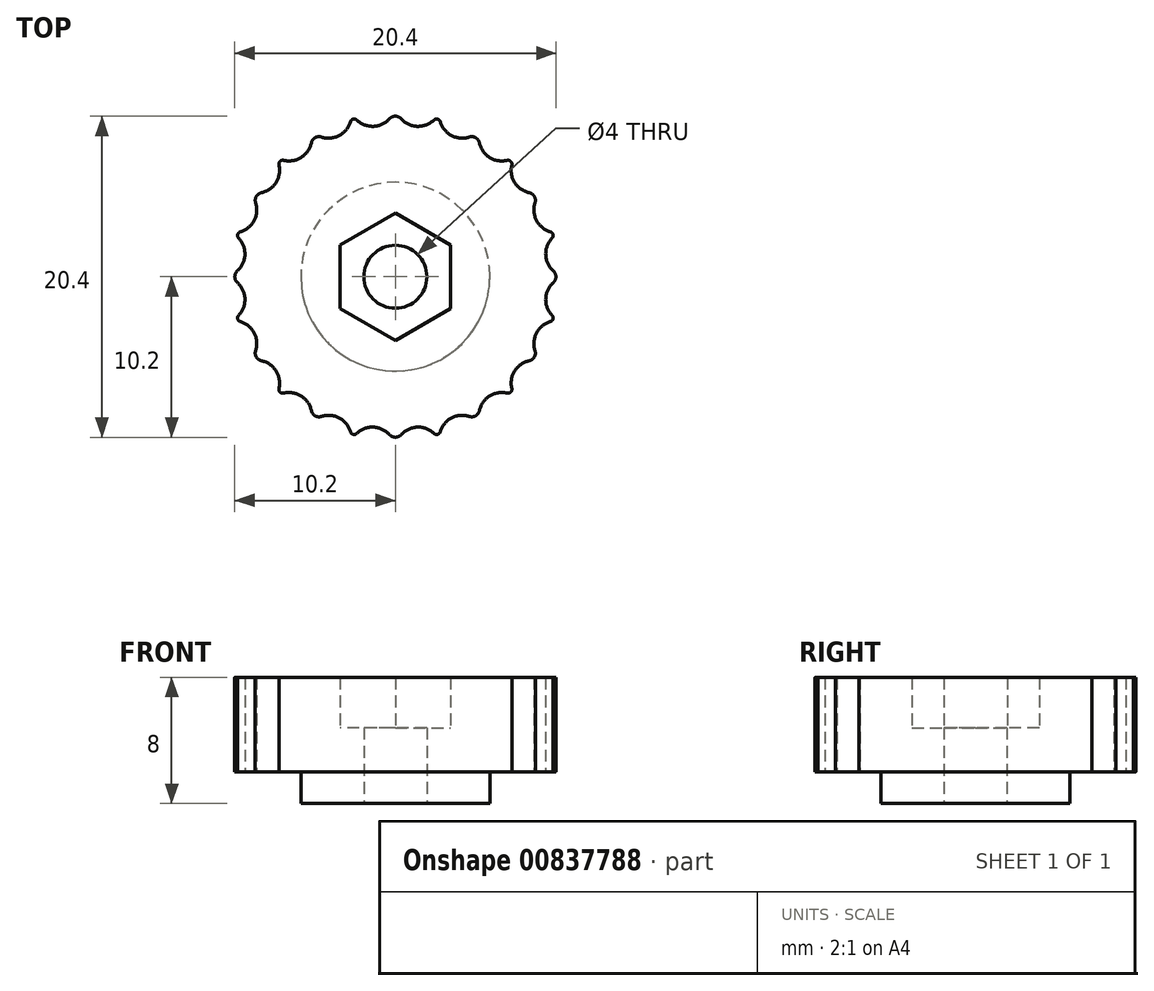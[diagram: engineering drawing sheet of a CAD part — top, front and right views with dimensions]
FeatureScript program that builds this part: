
annotation { "Feature Type Name" : "Feature", "Feature Type Description" : "" }
export const myFeature = defineFeature(function(context is Context, id is Id, definition is map)
    precondition{}
    {
        {
            var Q0;
            Q0=qCreatedBy(makeId("Top.planeOp"),FACE);
            var sketch = newSketch(context, id + "F0", { "sketchPlane" : qUnion([Q0])});
            skLineSegment(sketch, "E0", {"start": v(0, 0) * mm, "end": v(-11, 0) * mm});
            skLineSegment(sketch, "E1", {"start": v(0, 0) * mm, "end": v(0, 11) * mm});
            skLineSegment(sketch, "E2", {"start": v(0, 0) * mm, "end": v(-10.63, 2.85) * mm, "construction": true});
            skLineSegment(sketch, "E3", {"start": v(0, 0) * mm, "end": v(-9.53, 5.5) * mm, "construction": true});
            skLineSegment(sketch, "E4", {"start": v(0, 0) * mm, "end": v(-7.78, 7.78) * mm, "construction": true});
            skLineSegment(sketch, "E5", {"start": v(0, 0) * mm, "end": v(-2.85, 10.63) * mm, "construction": true});
            skLineSegment(sketch, "E6", {"start": v(0, 0) * mm, "end": v(-5.5, 9.53) * mm, "construction": true});
            skArc(sketch, "E7", {"start": v(-11, 0) * mm, "mid": v(-9.56, 1.26) * mm, "end": v(-10.63, 2.85) * mm});
            skArc(sketch, "E8", {"start": v(-7.78, 7.78) * mm, "mid": v(-5.87, 7.65) * mm, "end": v(-5.5, 9.53) * mm});
            skArc(sketch, "E9", {"start": v(-5.5, 9.53) * mm, "mid": v(-3.7, 8.91) * mm, "end": v(-2.85, 10.63) * mm});
            skArc(sketch, "E10", {"start": v(-2.85, 10.63) * mm, "mid": v(-1.26, 9.56) * mm, "end": v(0, 11) * mm});
            skArc(sketch, "E11", {"start": v(-10.63, 2.85) * mm, "mid": v(-8.91, 3.7) * mm, "end": v(-9.53, 5.5) * mm});
            skArc(sketch, "E12", {"start": v(-9.53, 5.5) * mm, "mid": v(-7.65, 5.87) * mm, "end": v(-7.78, 7.78) * mm});
            skLineSegment(sketch, "E13", {"start": v(0, 0) * mm, "end": v(-3.5, 0) * mm, "construction": true});
            skLineSegment(sketch, "E14", {"start": v(0, 0) * mm, "end": v(0, 4.04) * mm, "construction": true});
            skArc(sketch, "E15", {"start": v(0, 4.04) * mm, "mid": v(-2.86, 2.86) * mm, "end": v(-4.04, 0) * mm, "construction": true});
            skPoint(sketch, "E16", {"position": v(-3.5, 2.02) * mm});
            skLineSegment(sketch, "E17", {"start": v(0, 4.04) * mm, "end": v(-3.5, 2.02) * mm});
            skLineSegment(sketch, "E18", {"start": v(-3.5, 0) * mm, "end": v(-3.5, 2.02) * mm});
            skArc(sketch, "E19", {"start": v(0, 2) * mm, "mid": v(-1.41, 1.41) * mm, "end": v(-2, 0) * mm});
            skSolve(sketch);
        }
        {
            var Q0;
            {var subQ0=sQuery(id+"F0.wireOp",EDGE,"E7");Q0=makeQuery(id+"F0.imprint","IMPRINT",FACE,{"disambiguationData":[TD([[makeQuery(id+"F0.imprint","IMPRINT",EDGE,{"derivedFrom":subQ0}),-1.0]])]});}
            extrude(context, id + "F1", {"entities" : qUnion([Q0]), "depth" : 6 * mm, "offsetDistance" : 25 * mm});
        }
        {
            var Q0;
            {var subQ1=sQuery(id+"F0.wireOp",EDGE,"E17");Q0=makeQuery(id+"F0.imprint","IMPRINT",FACE,{"disambiguationData":[TD([[makeQuery(id+"F0.imprint","IMPRINT",EDGE,{"derivedFrom":subQ1}),1.0]])]});}
            extrude(context, id + "F2", {"entities" : qUnion([Q0]), "operationType" : NewBodyOperationType.ADD, "depth" : 2.8 * mm, "offsetDistance" : 25 * mm});
        }
        {
            var Q0;
            Q0=makeQuery(id+"F1.opExtrude","SWEPT_EDGE",EDGE,{"disambiguationData":[OSD([sQuery(id+"F0.wireOp",EDGE,"E9"),sQuery(id+"F0.wireOp",EDGE,"E10")])]});
            var Q1;
            Q1=makeQuery(id+"F1.opExtrude","SWEPT_EDGE",EDGE,{"disambiguationData":[OSD([sQuery(id+"F0.wireOp",EDGE,"E8"),sQuery(id+"F0.wireOp",EDGE,"E12")])]});
            var Q2;
            Q2=makeQuery(id+"F1.opExtrude","SWEPT_EDGE",EDGE,{"disambiguationData":[OSD([sQuery(id+"F0.wireOp",EDGE,"E7"),sQuery(id+"F0.wireOp",EDGE,"E11")])]});
            fillet(context, id + "F3", {"entities" : qUnion([Q0, Q1, Q2]), "radius" : .25 * mm, "tangentPropagation" : true, "allowEdgeOverflow" : false});
        }
        {
            var Q0;
            Q0=makeQuery(id+"F1.opExtrude","SWEPT_EDGE",EDGE,{"disambiguationData":[OSD([sQuery(id+"F0.wireOp",EDGE,"E8"),sQuery(id+"F0.wireOp",EDGE,"E9")])]});
            var Q1;
            Q1=makeQuery(id+"F1.opExtrude","SWEPT_EDGE",EDGE,{"disambiguationData":[OSD([sQuery(id+"F0.wireOp",EDGE,"E11"),sQuery(id+"F0.wireOp",EDGE,"E12")])]});
            fillet(context, id + "F4", {"entities" : qUnion([Q0, Q1]), "radius" : .5 * mm, "tangentPropagation" : true, "allowEdgeOverflow" : false});
        }
        {
            var Q0;
            Q0=makeQuery(id+"F1.opExtrude","SWEPT_BODY",BODY,{"disambiguationData":[OSD([sQuery(id+"F0.wireOp",EDGE,"E0"),sQuery(id+"F0.wireOp",EDGE,"E1"),sQuery(id+"F0.wireOp",EDGE,"E7"),sQuery(id+"F0.wireOp",EDGE,"E8"),sQuery(id+"F0.wireOp",EDGE,"E9"),sQuery(id+"F0.wireOp",EDGE,"E10"),sQuery(id+"F0.wireOp",EDGE,"E11"),sQuery(id+"F0.wireOp",EDGE,"E12"),sQuery(id+"F0.wireOp",EDGE,"E17"),sQuery(id+"F0.wireOp",EDGE,"E18")])]});
            var Q1;
            {var subQ0=sQuery(id+"F0.wireOp",EDGE,"E0");Q1=makeQuery(id+"F2.boolean.opBoolean","MERGE",FACE,{"derivedFrom":[makeQuery(id+"F1.opExtrude","SWEPT_FACE",FACE,{"disambiguationData":[OSD([subQ0])]}),makeQuery(id+"F2.opExtrude","SWEPT_FACE",FACE,{"disambiguationData":[OSD([subQ0])]})]});}
            mirror(context, id + "F5", {"operationType" : NewBodyOperationType.ADD, "entities" : qUnion([Q0]), "mirrorPlane" : qUnion([Q1])});
        }
        {
            var Q0;
            Q0=makeQuery(id+"F1.opExtrude","SWEPT_BODY",BODY,{"disambiguationData":[OSD([sQuery(id+"F0.wireOp",EDGE,"E0"),sQuery(id+"F0.wireOp",EDGE,"E1"),sQuery(id+"F0.wireOp",EDGE,"E7"),sQuery(id+"F0.wireOp",EDGE,"E8"),sQuery(id+"F0.wireOp",EDGE,"E9"),sQuery(id+"F0.wireOp",EDGE,"E10"),sQuery(id+"F0.wireOp",EDGE,"E11"),sQuery(id+"F0.wireOp",EDGE,"E12"),sQuery(id+"F0.wireOp",EDGE,"E17"),sQuery(id+"F0.wireOp",EDGE,"E18")])]});
            var Q1;
            {var subQ0=sQuery(id+"F0.wireOp",EDGE,"E1");Q1=makeQuery(id+"F5.opPattern","COPY",FACE,{"derivedFrom":makeQuery(id+"F2.boolean.opBoolean","MERGE",FACE,{"derivedFrom":[makeQuery(id+"F1.opExtrude","SWEPT_FACE",FACE,{"disambiguationData":[OSD([subQ0])]}),makeQuery(id+"F2.opExtrude","SWEPT_FACE",FACE,{"disambiguationData":[OSD([subQ0])]})]}),"instanceName":"1"});}
            mirror(context, id + "F6", {"operationType" : NewBodyOperationType.ADD, "entities" : qUnion([Q0]), "mirrorPlane" : qUnion([Q1])});
        }
        {
            var Q0;
            {var subQ0=makeQuery(id+"F5.opPattern","COPY",EDGE,{"derivedFrom":makeQuery(id+"F1.opExtrude","SWEPT_EDGE",EDGE,{"disambiguationData":[OSD([sQuery(id+"F0.wireOp",EDGE,"E1"),sQuery(id+"F0.wireOp",EDGE,"E10")])]}),"instanceName":"1"});Q0=makeQuery(id+"F6.boolean.opBoolean","MERGE",EDGE,{"derivedFrom":[subQ0,makeQuery(id+"F6.opPattern","COPY",EDGE,{"derivedFrom":subQ0,"instanceName":"1"})]});}
            var Q1;
            {var subQ0=makeQuery(id+"F1.opExtrude","SWEPT_EDGE",EDGE,{"disambiguationData":[OSD([sQuery(id+"F0.wireOp",EDGE,"E0"),sQuery(id+"F0.wireOp",EDGE,"E7")])]});Q1=makeQuery(id+"F6.opPattern","COPY",EDGE,{"derivedFrom":makeQuery(id+"F5.boolean.opBoolean","MERGE",EDGE,{"derivedFrom":[subQ0,makeQuery(id+"F5.opPattern","COPY",EDGE,{"derivedFrom":subQ0,"instanceName":"1"})]}),"instanceName":"1"});}
            var Q2;
            {var subQ0=makeQuery(id+"F1.opExtrude","SWEPT_EDGE",EDGE,{"disambiguationData":[OSD([sQuery(id+"F0.wireOp",EDGE,"E1"),sQuery(id+"F0.wireOp",EDGE,"E10")])]});Q2=makeQuery(id+"F6.boolean.opBoolean","MERGE",EDGE,{"derivedFrom":[subQ0,makeQuery(id+"F6.opPattern","COPY",EDGE,{"derivedFrom":subQ0,"instanceName":"1"})]});}
            var Q3;
            {var subQ0=makeQuery(id+"F1.opExtrude","SWEPT_EDGE",EDGE,{"disambiguationData":[OSD([sQuery(id+"F0.wireOp",EDGE,"E0"),sQuery(id+"F0.wireOp",EDGE,"E7")])]});Q3=makeQuery(id+"F5.boolean.opBoolean","MERGE",EDGE,{"derivedFrom":[subQ0,makeQuery(id+"F5.opPattern","COPY",EDGE,{"derivedFrom":subQ0,"instanceName":"1"})]});}
            fillet(context, id + "F7", {"entities" : qUnion([Q0, Q1, Q2, Q3]), "radius" : .5 * mm, "tangentPropagation" : true, "allowEdgeOverflow" : false});
        }
        {
            var Q0;
            {var subQ0=sQuery(id+"F0.wireOp",EDGE,"E18");var subQ1=sQuery(id+"F0.wireOp",EDGE,"E17");var subQ2=sQuery(id+"F0.wireOp",EDGE,"E1");var subQ3=sQuery(id+"F0.wireOp",EDGE,"E0");var subQ4=makeQuery(id+"F2.boolean.opBoolean","MERGE",FACE,{"derivedFrom":[makeQuery(id+"F1.opExtrude","CAP_FACE",FACE,{"disambiguationData":[OSD([subQ3,subQ2,sQuery(id+"F0.wireOp",EDGE,"E7"),sQuery(id+"F0.wireOp",EDGE,"E8"),sQuery(id+"F0.wireOp",EDGE,"E9"),sQuery(id+"F0.wireOp",EDGE,"E10"),sQuery(id+"F0.wireOp",EDGE,"E11"),sQuery(id+"F0.wireOp",EDGE,"E12"),subQ1,subQ0])],"isStart":true}),makeQuery(id+"F2.opExtrude","CAP_FACE",FACE,{"disambiguationData":[OSD([subQ3,subQ2,subQ1,subQ0,sQuery(id+"F0.wireOp",EDGE,"E19")])],"isStart":true})]});var subQ5=makeQuery(id+"F5.boolean.opBoolean","MERGE",FACE,{"derivedFrom":[subQ4,makeQuery(id+"F5.opPattern","COPY",FACE,{"derivedFrom":subQ4,"instanceName":"1"})]});Q0=makeQuery(id+"F6.boolean.opBoolean","MERGE",FACE,{"derivedFrom":[subQ5,makeQuery(id+"F6.opPattern","COPY",FACE,{"derivedFrom":subQ5,"instanceName":"1"})]});}
            var sketch = newSketch(context, id + "F8", { "sketchPlane" : qUnion([Q0])});
            skCircle(sketch, "E20", {"center": v(0, 0) * mm, "radius": 6 * mm});
            skSolve(sketch);
        }
        {
            var Q0;
            Q0=makeQuery(id+"F8.imprint","IMPRINT",FACE,{"disambiguationData":[TD([[makeQuery(id+"F8.imprint","IMPRINT",EDGE,{"derivedFrom":sQuery(id+"F8.wireOp",EDGE,"E20")}),1.0]])]});
            extrude(context, id + "F9", {"entities" : qUnion([Q0]), "operationType" : NewBodyOperationType.ADD, "depth" : 2 * mm, "offsetDistance" : 25 * mm});
        }
    });
